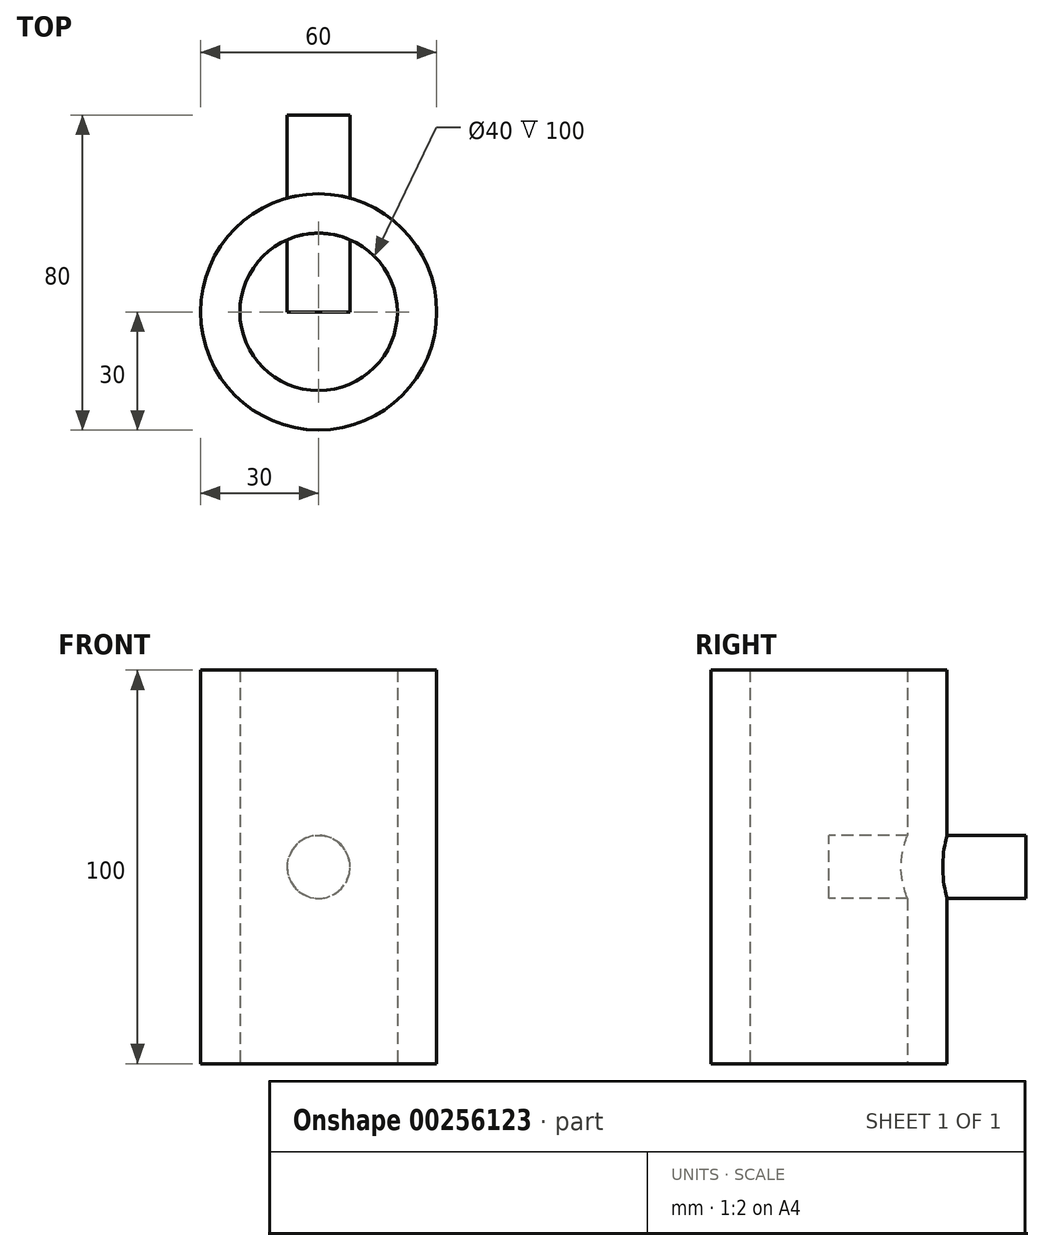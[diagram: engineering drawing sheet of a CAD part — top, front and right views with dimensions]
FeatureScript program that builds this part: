
annotation { "Feature Type Name" : "Feature", "Feature Type Description" : "" }
export const myFeature = defineFeature(function(context is Context, id is Id, definition is map)
    precondition{}
    {
        {
            var Q0;
            Q0=qCreatedBy(makeId("Top.planeOp"),FACE);
            var sketch = newSketch(context, id + "F0", { "sketchPlane" : qUnion([Q0])});
            skCircle(sketch, "E0", {"center": v(0, 0) * mm, "radius": 30 * mm});
            skCircle(sketch, "E1", {"center": v(0, 0) * mm, "radius": 20 * mm});
            skSolve(sketch);
        }
        {
            var Q0;
            Q0=makeQuery(id+"F0.imprint","IMPRINT",FACE,{"disambiguationData":[TD([[makeQuery(id+"F0.imprint","IMPRINT",EDGE,{"derivedFrom":sQuery(id+"F0.wireOp",EDGE,"E0")}),1.0]])]});
            extrude(context, id + "F1", {"entities" : qUnion([Q0]), "depth" : 100 * mm});
        }
        {
            var Q0;
            Q0=qCreatedBy(makeId("Front.planeOp"),FACE);
            var sketch = newSketch(context, id + "F2", { "sketchPlane" : qUnion([Q0])});
            skLineSegment(sketch, "E2", {"start": v(0, 0) * mm, "end": v(0, 50) * mm});
            skCircle(sketch, "E3", {"center": v(0, 50) * mm, "radius": 8 * mm});
            skSolve(sketch);
        }
        {
            var Q0;
            Q0=makeQuery(id+"F2.imprint","IMPRINT",FACE,{"disambiguationData":[TD([[makeQuery(id+"F2.imprint","IMPRINT",EDGE,{"derivedFrom":sQuery(id+"F2.wireOp",EDGE,"E3")}),1.0]])]});
            extrude(context, id + "F3", {"entities" : qUnion([Q0]), "operationType" : NewBodyOperationType.ADD, "oppositeDirection" : true, "depth" : 50 * mm});
        }
    });
